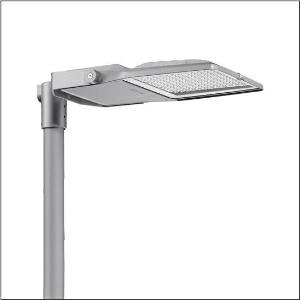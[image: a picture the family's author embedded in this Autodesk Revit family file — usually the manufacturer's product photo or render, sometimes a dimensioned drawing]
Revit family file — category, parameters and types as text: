
# Revit family: floodlight_fl_21_iq_midi___pl33t_5xa7782f2f3a_348f
name_source: partatom
category: Lighting Fixtures
units: mm (PartAtom-declared; Revit-internal decimal feet)

## family parameters
Cut with Voids When Loaded = No
Host = Face
Light Source = No
Part Type = Normal
Room Calculation Point = No
Round Connector Dimension = Use Diameter
Shared = No

## types (1)
- --- (1 x LED, 35350 lm, 270.2 W, 3000K)
    Apparent Load = 270 VA
    CIE Flux Codes = 26 75 99 100 100
    Color Rendering = 70
    Color Temperature = 3000K
    Default Elevation = 1800 mm
    Description = Floodlight FL 21 iQ midi, floodlight, primary light control with lens, of PMMA, primary optical cover: protective disc, of toughened safety glass, transparent, light distribution: PL33T, light emission: direct distribution, installation type: surface-mounted, LED, High Power LED, rated luminous flux: 35.350lm, luminous efficacy: 131lm/W, light colour: 730, colour temperature: 3000K, control gear: ECG iQ, control: optimised constant luminous flux control (CLO 2.0), Desk-Remote (wireless, voltage-free reading and setting of iQ features in the workshop via application-optimized NFC function/RFID function), Smart-Wire, Night-Set, Temp-Guard, Auto-Match, Street-Remote, with terminal, 6-pole, mains connection: 220..240V, AC, 50/60Hz, start of lifetime: 270W, end of service life: 287W, reduction: 117W, luminaire housing, of diecast aluminium, powder-coated, Siteco® metallic grey (DB 702S), corrosivity category C5 mid according to DIN EN ISO 12944, sealing non-destructively replaceable, please order mast flange separately, mast bracket, of steel, galvanised, powder-coated, Siteco® metallic grey (DB 702S), protection rating (complete): IP66, insulation class (complete): insulation class II (safety insulation), certification: CE, protection symbol: D, impact resistance: IK08, permissible operating ambient temperature: -40..+40°C, permissible operating ambient temperature for outdoor applications: -40..+50°C, standard: DIN EN 12944, LABS conformity tested according to VDMA 24364:2018-05, packaging unit: 1 piece

Light Distribution: PL33T
    Height = 76 mm
    Lamp = 1 x LED
    Lamp Light Flux = 35350 lm
    Lamp Power = 270.2 W
    Lamp count = 1
    Length = 657 mm
    Luminous efficacy = 131 lm/W
    Manufacturer = Siteco
    ModVariant = No
    Model = 5XA7782F2F3A
    Number of Poles = 1
    OnlyDefault = Yes
    Power Factor = 1
    Product Name = Floodlight FL 21 iQ midi | PL33T
    Product group = floodlight | pylon annexe
    ProductGroupID = 6200
    Protection Class = Protection class II
    Protection Degree = IP 66
    RLX_Detail_Level = 1
    RLX_Emergency_Light_Flux = 0 lm
    RLX_Emergency_Type = 0
    RLX_Emergency_Type_DB = No
    RlxData = <blob elided: 153461 chars, md5=9c649147>
    Socket = socket
    Standby Power = 0 W
    System Light Flux = 35350 lm
    System Power = 270 W
    Type Comments = factory setting: luminous flux: 100 % | dim-lin: 254 | 620 mA
    Type Image = l_1007123.jpg
    URL = http://relux.com
    VarID = @adj_033501
    Voltage = 0 V
    Weight = 0.00 kg
    Width = 442 mm

## geometry (parser evidence)
native form markers: Blend x4, Sweep x13
no freeform markers — native parametric forms only
